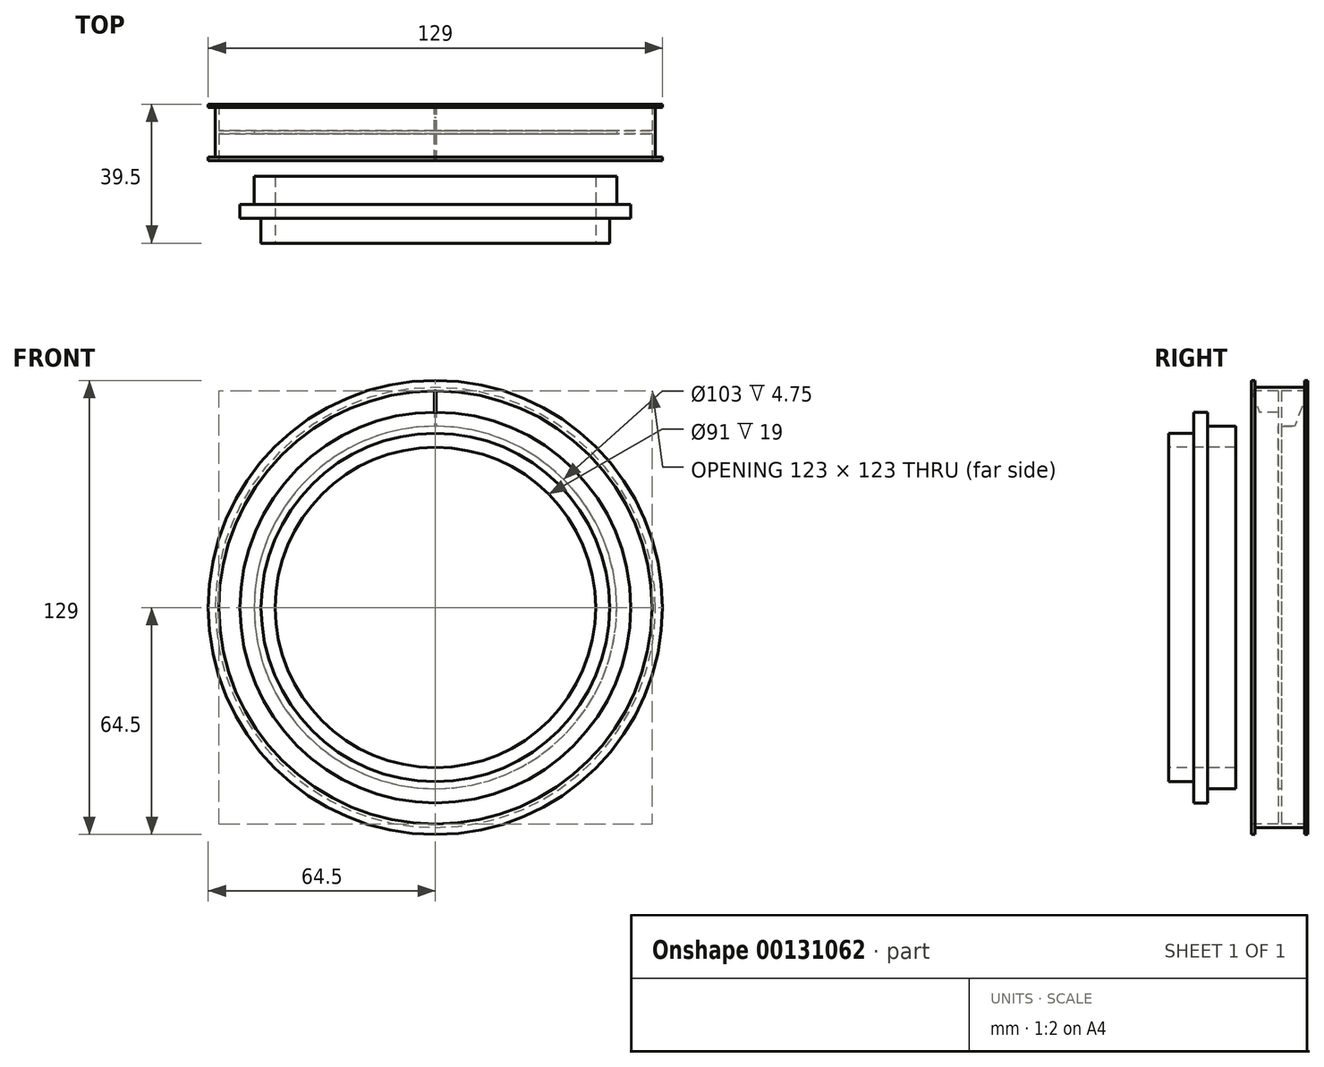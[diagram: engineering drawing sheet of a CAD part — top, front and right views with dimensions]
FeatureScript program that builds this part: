
annotation { "Feature Type Name" : "Feature", "Feature Type Description" : "" }
export const myFeature = defineFeature(function(context is Context, id is Id, definition is map)
    precondition{}
    {
        {
            var Q0;
            Q0=qCreatedBy(makeId("Right.planeOp"),FACE);
            var sketch = newSketch(context, id + "F0", { "sketchPlane" : qUnion([Q0])});
            skLineSegment(sketch, "E0", {"start": v(-69.51, 0) * mm, "end": v(82.98, 0) * mm, "construction": true});
            skLineSegment(sketch, "E1", {"start": v(-11, 45.5) * mm, "end": v(8, 45.5) * mm});
            skLineSegment(sketch, "E2", {"start": v(8, 45.5) * mm, "end": v(8, 51.5) * mm});
            skLineSegment(sketch, "E3", {"start": v(8, 51.5) * mm, "end": v(0, 51.5) * mm});
            skLineSegment(sketch, "E4", {"start": v(0, 51.5) * mm, "end": v(0, 55.5) * mm});
            skLineSegment(sketch, "E5", {"start": v(0, 55.5) * mm, "end": v(-4, 55.5) * mm});
            skLineSegment(sketch, "E6", {"start": v(-4, 55.5) * mm, "end": v(-4, 49.5) * mm});
            skLineSegment(sketch, "E7", {"start": v(-4, 49.5) * mm, "end": v(-11, 49.5) * mm});
            skLineSegment(sketch, "E8", {"start": v(-11, 49.5) * mm, "end": v(-11, 45.5) * mm});
            skLineSegment(sketch, "E9", {"start": v(0, -10.36) * mm, "end": v(0, 72.42) * mm, "construction": true});
            skSolve(sketch);
        }
        {
            var Q0;
            Q0 = qSketchRegion(id + "F0", true);
            var Q1;
            Q1=sQuery(id+"F0.wireOp",EDGE,"E0");
            revolve(context, id + "F1", {"entities" : qUnion([Q0]), "axis" : qUnion([Q1]), "revolveType" : RevolveType.FULL});
        }
        {
            var Q0;
            Q0=qCreatedBy(makeId("Right.planeOp"),FACE);
            var sketch = newSketch(context, id + "F2", { "sketchPlane" : qUnion([Q0])});
            skLineSegment(sketch, "E10", {"start": v(-52.99, 0) * mm, "end": v(53.2, 0) * mm, "construction": true});
            skLineSegment(sketch, "E11", {"start": v(0, 56.15) * mm, "end": v(0, -56.8) * mm, "construction": true});
            skLineSegment(sketch, "E12", {"start": v(20, 51.5) * mm, "end": v(21, 51.5) * mm});
            skLineSegment(sketch, "E13", {"start": v(21, 61.5) * mm, "end": v(28.5, 61.5) * mm});
            skLineSegment(sketch, "E14", {"start": v(28.5, 61.5) * mm, "end": v(28.5, 64.5) * mm});
            skLineSegment(sketch, "E15", {"start": v(28.5, 64.5) * mm, "end": v(27.5, 64.5) * mm});
            skLineSegment(sketch, "E16", {"start": v(27.5, 64.5) * mm, "end": v(27.5, 62.5) * mm});
            skLineSegment(sketch, "E17", {"start": v(27.5, 62.5) * mm, "end": v(13.5, 62.5) * mm});
            skLineSegment(sketch, "E18", {"start": v(13.5, 62.5) * mm, "end": v(13.5, 64.5) * mm});
            skLineSegment(sketch, "E19", {"start": v(13.5, 64.5) * mm, "end": v(12.5, 64.5) * mm});
            skLineSegment(sketch, "E20", {"start": v(12.5, 64.5) * mm, "end": v(12.5, 61.5) * mm});
            skLineSegment(sketch, "E21", {"start": v(12.5, 61.5) * mm, "end": v(20, 61.5) * mm});
            skLineSegment(sketch, "E22", {"start": v(20, 61.5) * mm, "end": v(20, 51.5) * mm});
            skLineSegment(sketch, "E23", {"start": v(20.5, 73.61) * mm, "end": v(20.5, 49.08) * mm, "construction": true});
            skLineSegment(sketch, "E24", {"start": v(21, 61.5) * mm, "end": v(21, 51.5) * mm});
            skSolve(sketch);
        }
        {
            var Q0;
            Q0 = qSketchRegion(id + "F2", true);
            var Q1;
            Q1=sQuery(id+"F2.wireOp",EDGE,"E10");
            revolve(context, id + "F3", {"entities" : qUnion([Q0]), "axis" : qUnion([Q1]), "revolveType" : RevolveType.FULL});
        }
        {
            var Q0;
            Q0=qCreatedBy(makeId("Right.planeOp"),FACE);
            var sketch = newSketch(context, id + "F4", { "sketchPlane" : qUnion([Q0])});
            skLineSegment(sketch, "E25", {"start": v(12.5, 61.5) * mm, "end": v(20, 41.5) * mm});
            skLineSegment(sketch, "E26", {"start": v(12.5, 61.5) * mm, "end": v(20, 61.5) * mm});
            skLineSegment(sketch, "E27", {"start": v(20, 61.5) * mm, "end": v(20, 41.5) * mm});
            skLineSegment(sketch, "E28", {"start": v(20.5, 66.89) * mm, "end": v(20.5, 6.83) * mm, "construction": true});
            skLineSegment(sketch, "E29", {"start": v(0, -6.02) * mm, "end": v(0, 62.34) * mm, "construction": true});
            skLineSegment(sketch, "E30", {"start": v(-33.18, 0) * mm, "end": v(61.26, 0) * mm, "construction": true});
            skLineSegment(sketch, "E31.MirrorCS", {"start": v(28.5, 61.5) * mm, "end": v(21, 41.5) * mm});
            skLineSegment(sketch, "E32.MirrorCS", {"start": v(28.5, 61.5) * mm, "end": v(21, 61.5) * mm});
            skLineSegment(sketch, "E33.MirrorCS", {"start": v(21, 61.5) * mm, "end": v(21, 41.5) * mm});
            skSolve(sketch);
        }
        {
            var Q0;
            Q0 = qSketchRegion(id + "F4", true);
            extrude(context, id + "F5", {"entities" : qUnion([Q0]), "operationType" : NewBodyOperationType.ADD, "endBound" : BoundingType.SYMMETRIC, "depth" : 0.5 * mm});
        }
        {
            var Q0;
            Q0=qCreatedBy(makeId("Front.planeOp"),FACE);
            cPlane(context, id + "F6", {"entities" : qUnion([Q0]), "cplaneType" : CPlaneType.OFFSET, "offset" : 10 * mm, "oppositeDirection" : true, "width" : 150 * mm, "height" : 150 * mm});
        }
        {
            var Q0;
            Q0=qCreatedBy(id+"F6.planeOp",FACE);
            var sketch = newSketch(context, id + "F7", { "sketchPlane" : qUnion([Q0])});
            skCircle(sketch, "E34", {"center": v(0, 0) * mm, "radius": 55.5 * mm});
            skSolve(sketch);
        }
        {
            var Q0;
            Q0 = qSketchRegion(id + "F7", true);
            var Q1;
            {var subQ0=sQuery(id+"F4.wireOp",EDGE,"E27");var subQ1=makeQuery(id+"F5.opExtrude","SWEPT_FACE",FACE,{"disambiguationData":[OSD([subQ0])]});var subQ2=sQuery(id+"F4.wireOp",EDGE,"E26");var subQ3=sQuery(id+"F4.wireOp",EDGE,"E25");var subQ4=makeQuery(id+"F5.opExtrude","CAP_FACE",FACE,{"disambiguationData":[OSD([subQ3,subQ2,subQ0])],"isStart":true});Q1=makeQuery(id+"FmRF89iO4RahQIt_2.11.F5.boolean.opBoolean","SPLIT",FACE,{"disambiguationData":[TD([subQ1])],"derivedFrom":makeQuery(id+"FmRF89iO4RahQIt_2.10.F5.boolean.opBoolean","SPLIT",FACE,{"disambiguationData":[TD([subQ1])],"derivedFrom":makeQuery(id+"FmRF89iO4RahQIt_2.9.F5.boolean.opBoolean","SPLIT",FACE,{"disambiguationData":[TD([subQ1])],"derivedFrom":makeQuery(id+"FmRF89iO4RahQIt_2.8.F5.boolean.opBoolean","SPLIT",FACE,{"disambiguationData":[TD([subQ1])],"derivedFrom":makeQuery(id+"FmRF89iO4RahQIt_2.7.F5.boolean.opBoolean","SPLIT",FACE,{"disambiguationData":[TD([subQ1])],"derivedFrom":makeQuery(id+"FmRF89iO4RahQIt_2.6.F5.boolean.opBoolean","SPLIT",FACE,{"disambiguationData":[TD([subQ1])],"derivedFrom":makeQuery(id+"FmRF89iO4RahQIt_2.5.F5.boolean.opBoolean","SPLIT",FACE,{"disambiguationData":[TD([subQ1])],"derivedFrom":makeQuery(id+"FmRF89iO4RahQIt_2.4.F5.boolean.opBoolean","SPLIT",FACE,{"disambiguationData":[TD([subQ1])],"derivedFrom":makeQuery(id+"FmRF89iO4RahQIt_2.3.F5.boolean.opBoolean","SPLIT",FACE,{"disambiguationData":[TD([subQ1])],"derivedFrom":makeQuery(id+"FmRF89iO4RahQIt_2.2.F5.boolean.opBoolean","SPLIT",FACE,{"disambiguationData":[TD([subQ1])],"derivedFrom":makeQuery(id+"FmRF89iO4RahQIt_2.1.F5.boolean.opBoolean","SPLIT",FACE,{"disambiguationData":[TD([subQ4])],"derivedFrom":makeQuery(id+"F3.opRevolve","SWEPT_FACE",FACE,{"disambiguationData":[OSD([sQuery(id+"F2.wireOp",EDGE,"E22")])]})})})})})})})})})})})});}
            extrude(context, id + "F8", {"entities" : qUnion([Q0]), "operationType" : NewBodyOperationType.REMOVE, "endBound" : BoundingType.UP_TO_SURFACE, "oppositeDirection" : true, "endBoundEntityFace" : qUnion([Q1]), "depth" : 25 * mm});
        }
        {
            var Q0;
            Q0=qCreatedBy(makeId("Front.planeOp"),FACE);
            cPlane(context, id + "F9", {"entities" : qUnion([Q0]), "cplaneType" : CPlaneType.OFFSET, "offset" : 55 * mm, "oppositeDirection" : true, "width" : 150 * mm, "height" : 150 * mm});
        }
        {
            var Q0;
            Q0=qCreatedBy(id+"F9.planeOp",FACE);
            var sketch = newSketch(context, id + "F10", { "sketchPlane" : qUnion([Q0])});
            skCircle(sketch, "E35", {"center": v(0, 0) * mm, "radius": 51.5 * mm});
            skSolve(sketch);
        }
        {
            var Q0;
            Q0 = qSketchRegion(id + "F10", true);
            var Q1;
            {var subQ0=sQuery(id+"F4.wireOp",EDGE,"E33.MirrorCS");var subQ1=sQuery(id+"F4.wireOp",EDGE,"E32.MirrorCS");var subQ2=sQuery(id+"F4.wireOp",EDGE,"E31.MirrorCS");Q1=makeQuery(id+"FmRF89iO4RahQIt_2.1.F5.boolean.opBoolean","SPLIT",FACE,{"disambiguationData":[TD([makeQuery(id+"F5.opExtrude","CAP_FACE",FACE,{"disambiguationData":[OSD([subQ2,subQ1,subQ0])],"isStart":false})])],"derivedFrom":makeQuery(id+"F3.opRevolve","SWEPT_FACE",FACE,{"disambiguationData":[OSD([sQuery(id+"F2.wireOp",EDGE,"E24")])]})});}
            extrude(context, id + "F11", {"entities" : qUnion([Q0]), "operationType" : NewBodyOperationType.REMOVE, "endBound" : BoundingType.UP_TO_SURFACE, "endBoundEntityFace" : qUnion([Q1]), "depth" : 25 * mm});
        }
    });
